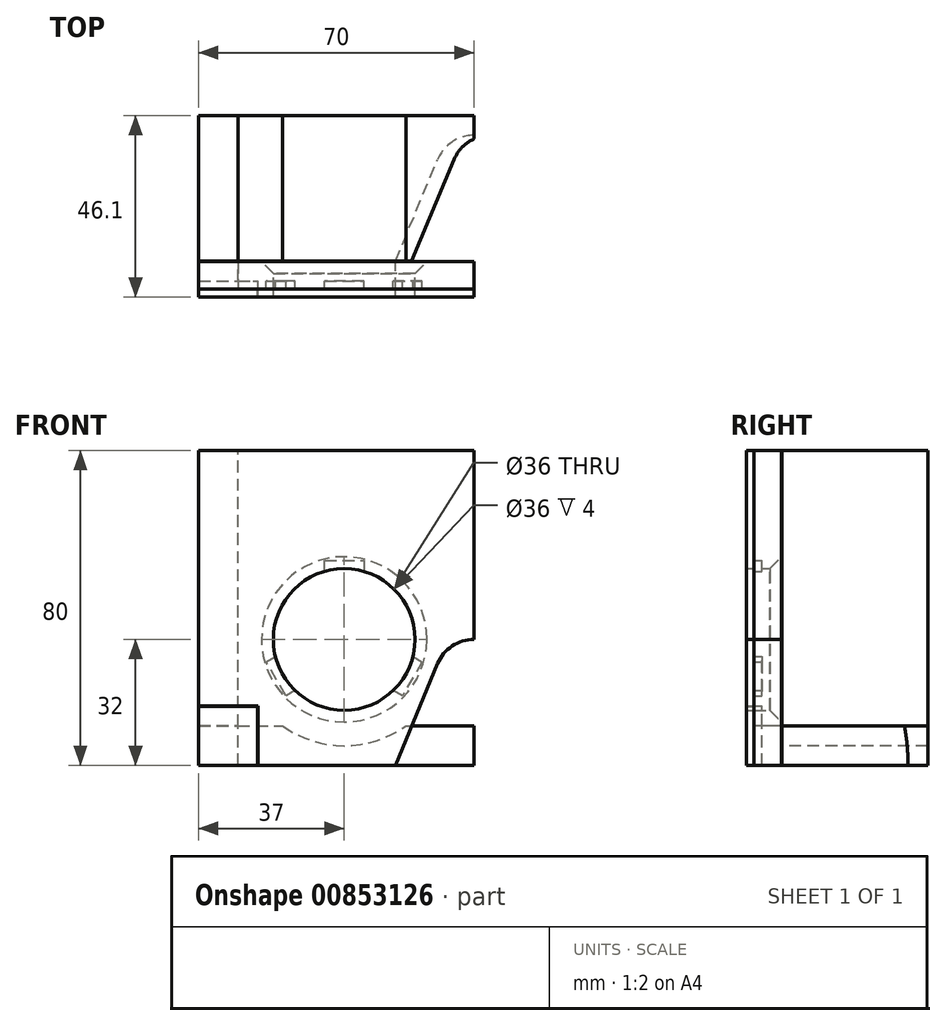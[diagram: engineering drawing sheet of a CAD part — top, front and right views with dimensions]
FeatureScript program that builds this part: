
annotation { "Feature Type Name" : "Feature", "Feature Type Description" : "" }
export const myFeature = defineFeature(function(context is Context, id is Id, definition is map)
    precondition{}
    {
        {
            assignVariable(context, id + "F0", {"name" : "tollerance", "anyValue" : 0.1});
        }
        {
            var Q0;
            Q0=qCreatedBy(makeId("Front.planeOp"),FACE);
            var sketch = newSketch(context, id + "F1", { "sketchPlane" : qUnion([Q0])});
            skCircle(sketch, "E0", {"center": v(-33, 0) * mm, "radius": 18 * mm});
            skCircle(sketch, "E1", {"center": v(33, 0) * mm, "radius": 18 * mm});
            skLineSegment(sketch, "E2", {"start": v(-33, 0) * mm, "end": v(0, 0) * mm, "construction": true});
            skLineSegment(sketch, "E3", {"start": v(0, 0) * mm, "end": v(33, 0) * mm, "construction": true});
            skSolve(sketch);
        }
        {
            var Q0;
            Q0=qCreatedBy(makeId("Front.planeOp"),FACE);
            var sketch = newSketch(context, id + "F2", { "sketchPlane" : qUnion([Q0])});
            skCircle(sketch, "E4", {"center": v(-33, 0) * mm, "radius": 18 * mm});
            skLineSegment(sketch, "E5", {"start": v(-38, 17.3) * mm, "end": v(-38, 20) * mm});
            skLineSegment(sketch, "E6", {"start": v(-38, 20) * mm, "end": v(-33, 20) * mm});
            skLineSegment(sketch, "E7", {"start": v(-33, 20) * mm, "end": v(-28, 20) * mm});
            skLineSegment(sketch, "E8", {"start": v(-28, 20) * mm, "end": v(-28, 17.3) * mm});
            skLineSegment(sketch, "E9.1.0", {"start": v(-45.47, -12.98) * mm, "end": v(-47.82, -14.33) * mm});
            skLineSegment(sketch, "E9.1.1", {"start": v(-47.82, -14.33) * mm, "end": v(-50.32, -10) * mm});
            skLineSegment(sketch, "E9.1.2", {"start": v(-50.32, -10) * mm, "end": v(-52.82, -5.67) * mm});
            skLineSegment(sketch, "E9.1.3", {"start": v(-52.82, -5.67) * mm, "end": v(-50.47, -4.32) * mm});
            skLineSegment(sketch, "E9.2.0", {"start": v(-15.53, -4.32) * mm, "end": v(-13.18, -5.67) * mm});
            skLineSegment(sketch, "E9.2.1", {"start": v(-13.18, -5.67) * mm, "end": v(-15.68, -10) * mm});
            skLineSegment(sketch, "E9.2.2", {"start": v(-15.68, -10) * mm, "end": v(-18.18, -14.33) * mm});
            skLineSegment(sketch, "E9.2.3", {"start": v(-18.18, -14.33) * mm, "end": v(-20.53, -12.98) * mm});
            skLineSegment(sketch, "E10", {"start": v(0, 48) * mm, "end": v(-70, 48) * mm});
            skLineSegment(sketch, "E11", {"start": v(-70, 48) * mm, "end": v(-70, -32) * mm});
            skLineSegment(sketch, "E12", {"start": v(-70, -32) * mm, "end": v(-26.67, -32) * mm});
            skArc(sketch, "E13", {"start": v(-26.67, -32) * mm, "mid": v(-21.12, -30.32) * mm, "end": v(-17.44, -25.85) * mm, "construction": true});
            skLineSegment(sketch, "E14", {"start": v(-17.44, -25.85) * mm, "end": v(-9.23, -6.15) * mm});
            skArc(sketch, "E15", {"start": v(0, 0) * mm, "mid": v(-5.55, -1.68) * mm, "end": v(-9.23, -6.15) * mm});
            skLineSegment(sketch, "E16", {"start": v(-17.44, -25.85) * mm, "end": v(-20, -32) * mm});
            skLineSegment(sketch, "E17.bottom", {"start": v(-70, -32) * mm, "end": v(-60, -32) * mm});
            skLineSegment(sketch, "E17.top", {"start": v(-70, -22) * mm, "end": v(-60, -22) * mm});
            skLineSegment(sketch, "E17.left", {"start": v(-70, -32) * mm, "end": v(-70, -22) * mm});
            skLineSegment(sketch, "E17.right", {"start": v(-60, -32) * mm, "end": v(-60, -22) * mm});
            skLineSegment(sketch, "E18", {"start": v(0, 0) * mm, "end": v(0, 48) * mm});
            skLineSegment(sketch, "E19.bottom", {"start": v(-70, -32) * mm, "end": v(-59.9, -32) * mm});
            skLineSegment(sketch, "E19.top", {"start": v(-70, -21.9) * mm, "end": v(-59.9, -21.9) * mm});
            skLineSegment(sketch, "E19.left", {"start": v(-70, -32) * mm, "end": v(-70, -21.9) * mm});
            skLineSegment(sketch, "E19.right", {"start": v(-59.9, -32) * mm, "end": v(-59.9, -21.9) * mm});
            skLineSegment(sketch, "E20", {"start": v(-26.67, -32) * mm, "end": v(-20, -32) * mm});
            skSolve(sketch);
        }
        {
            var Q0;
            {var subQ6=sQuery(id+"F2.wireOp",EDGE,"E5");Q0=makeQuery(id+"F2.imprint","IMPRINT",FACE,{"disambiguationData":[TD([[makeQuery(id+"F2.imprint","IMPRINT",EDGE,{"derivedFrom":subQ6}),1.0]])]});}
            extrude(context, id + "F3", {"entities" : qUnion([Q0]), "depth" : 2 * mm, "offsetDistance" : 25 * mm});
        }
        {
            var Q0;
            {var subQ6=sQuery(id+"F2.wireOp",EDGE,"E5");Q0=makeQuery(id+"F2.imprint","IMPRINT",FACE,{"disambiguationData":[TD([[makeQuery(id+"F2.imprint","IMPRINT",EDGE,{"derivedFrom":subQ6}),1.0]])]});}
            var Q1;
            {var subQ0=sQuery(id+"F2.wireOp",EDGE,"E9.1.0");Q1=makeQuery(id+"F2.imprint","IMPRINT",FACE,{"disambiguationData":[TD([[makeQuery(id+"F2.imprint","IMPRINT",EDGE,{"derivedFrom":subQ0}),-1.0]])]});}
            var Q2;
            {var subQ0=sQuery(id+"F2.wireOp",EDGE,"E9.2.0");Q2=makeQuery(id+"F2.imprint","IMPRINT",FACE,{"disambiguationData":[TD([[makeQuery(id+"F2.imprint","IMPRINT",EDGE,{"derivedFrom":subQ0}),-1.0]])]});}
            var Q3;
            {var subQ0=sQuery(id+"F2.wireOp",EDGE,"E5");Q3=makeQuery(id+"F2.imprint","IMPRINT",FACE,{"disambiguationData":[TD([[makeQuery(id+"F2.imprint","IMPRINT",EDGE,{"derivedFrom":subQ0}),-1.0]])]});}
            extrude(context, id + "F4", {"entities" : qUnion([Q0, Q1, Q2, Q3]), "operationType" : NewBodyOperationType.ADD, "oppositeDirection" : true, "depth" : 5 * mm, "offsetDistance" : 25 * mm});
        }
        {
            var Q0;
            {var subQ6=sQuery(id+"F2.wireOp",EDGE,"E5");Q0=makeQuery(id+"F2.imprint","IMPRINT",FACE,{"disambiguationData":[TD([[makeQuery(id+"F2.imprint","IMPRINT",EDGE,{"derivedFrom":subQ6}),1.0]])]});}
            var Q1;
            {var subQ0=sQuery(id+"F2.wireOp",EDGE,"E9.1.0");Q1=makeQuery(id+"F2.imprint","IMPRINT",FACE,{"disambiguationData":[TD([[makeQuery(id+"F2.imprint","IMPRINT",EDGE,{"derivedFrom":subQ0}),-1.0]])]});}
            var Q2;
            {var subQ0=sQuery(id+"F2.wireOp",EDGE,"E9.2.0");Q2=makeQuery(id+"F2.imprint","IMPRINT",FACE,{"disambiguationData":[TD([[makeQuery(id+"F2.imprint","IMPRINT",EDGE,{"derivedFrom":subQ0}),-1.0]])]});}
            var Q3;
            {var subQ0=sQuery(id+"F2.wireOp",EDGE,"E5");Q3=makeQuery(id+"F2.imprint","IMPRINT",FACE,{"disambiguationData":[TD([[makeQuery(id+"F2.imprint","IMPRINT",EDGE,{"derivedFrom":subQ0}),-1.0]])]});}
            extrude(context, id + "F5", {"entities" : qUnion([Q0, Q1, Q2, Q3]), "depth" : 4 * mm, "offsetDistance" : 25 * mm, "hasSecondDirection" : true, "secondDirectionOppositeDirection" : false, "secondDirectionDepth" : 2 * mm});
        }
        {
            var Q0;
            Q0=makeQuery(id+"FISosbWUcZb33Zc_2.opPattern","COPY",EDGE,{"derivedFrom":makeQuery(id+"F4.opExtrude","CAP_EDGE",EDGE,{"disambiguationData":[OSD([sQuery(id+"F2.wireOp",EDGE,"E4")])],"isStart":false}),"instanceName":"1"});
            var Q1;
            Q1=makeQuery(id+"F4.opExtrude","CAP_EDGE",EDGE,{"disambiguationData":[OSD([sQuery(id+"F2.wireOp",EDGE,"E4")])],"isStart":false});
            chamfer(context, id + "F6", {"entities" : qUnion([Q0, Q1]), "width" : 3 * mm, "tangentPropagation" : true});
        }
        {
            var Q0;
            Q0=qCreatedBy(makeId("Front.planeOp"),FACE);
            var sketch = newSketch(context, id + "F7", { "sketchPlane" : qUnion([Q0])});
            skLineSegment(sketch, "E21.bottom", {"start": v(-70, -32) * mm, "end": v(-55, -32) * mm});
            skLineSegment(sketch, "E21.top", {"start": v(-70, -17) * mm, "end": v(-55, -17) * mm});
            skLineSegment(sketch, "E21.left", {"start": v(-70, -32) * mm, "end": v(-70, -17) * mm});
            skLineSegment(sketch, "E21.right", {"start": v(-55, -32) * mm, "end": v(-55, -17) * mm});
            skLineSegment(sketch, "E22.bottom", {"start": v(-70, -32) * mm, "end": v(-54.9, -32) * mm});
            skLineSegment(sketch, "E22.top", {"start": v(-70, -16.9) * mm, "end": v(-54.9, -16.9) * mm});
            skLineSegment(sketch, "E22.left", {"start": v(-70, -32) * mm, "end": v(-70, -16.9) * mm});
            skLineSegment(sketch, "E22.right", {"start": v(-54.9, -32) * mm, "end": v(-54.9, -16.9) * mm});
            skSolve(sketch);
        }
        {
            var Q0;
            Q0=makeQuery(id+"F7.imprint","IMPRINT",FACE,{"disambiguationData":[TD([[makeQuery(id+"F7.imprint","IMPRINT",EDGE,{"derivedFrom":sQuery(id+"F7.wireOp",EDGE,"E21.bottom")}),1.0]])]});
            var Q1;
            Q1=makeQuery(id+"F7.imprint","IMPRINT",FACE,{"disambiguationData":[TD([[makeQuery(id+"F7.imprint","IMPRINT",EDGE,{"derivedFrom":sQuery(id+"F7.wireOp",EDGE,"E21.top")}),1.0]])]});
            extrude(context, id + "F8", {"entities" : qUnion([Q0, Q1]), "operationType" : NewBodyOperationType.REMOVE, "depth" : 4 * mm, "offsetDistance" : 25 * mm});
        }
        {
            var Q0;
            Q0=makeQuery(id+"F7.imprint","IMPRINT",FACE,{"disambiguationData":[TD([[makeQuery(id+"F7.imprint","IMPRINT",EDGE,{"derivedFrom":sQuery(id+"F7.wireOp",EDGE,"E21.bottom")}),1.0]])]});
            extrude(context, id + "F9", {"entities" : qUnion([Q0]), "depth" : 4 * mm, "offsetDistance" : 25 * mm, "hasSecondDirection" : true, "secondDirectionOppositeDirection" : false, "secondDirectionDepth" : 2 * mm});
        }
        {
            var Q0;
            {var subQ0=sQuery(id+"F2.wireOp",EDGE,"E17.top");Q0=makeQuery(id+"F2.imprint","IMPRINT",FACE,{"disambiguationData":[TD([[makeQuery(id+"F2.imprint","IMPRINT",EDGE,{"derivedFrom":subQ0}),-1.0]])]});}
            extrude(context, id + "F10", {"entities" : qUnion([Q0]), "operationType" : NewBodyOperationType.ADD, "oppositeDirection" : true, "depth" : (5 + getVariable(context, 'tollerance')) * mm, "offsetDistance" : 25 * mm, "hasSecondDirection" : true, "secondDirectionOppositeDirection" : false, "secondDirectionDepth" : 2 * mm});
        }
        {
            var Q0;
            Q0=makeQuery(id+"F10.opExtrude","CAP_FACE",FACE,{"disambiguationData":[OSD([sQuery(id+"F2.wireOp",EDGE,"E17.top"),sQuery(id+"F2.wireOp",EDGE,"E17.right"),sQuery(id+"F2.wireOp",EDGE,"E19.bottom"),sQuery(id+"F2.wireOp",EDGE,"E19.left")])],"isStart":false});
            var sketch = newSketch(context, id + "F11", { "sketchPlane" : qUnion([Q0])});
            skLineSegment(sketch, "E23.bottom", {"start": v(70, -32) * mm, "end": v(60, -32) * mm});
            skLineSegment(sketch, "E23.top", {"start": v(70, 48) * mm, "end": v(60, 48) * mm});
            skLineSegment(sketch, "E23.left", {"start": v(70, -32) * mm, "end": v(70, 48) * mm});
            skLineSegment(sketch, "E23.right", {"start": v(60, -32) * mm, "end": v(60, 48) * mm});
            skLineSegment(sketch, "E24.bottom", {"start": v(60, -32) * mm, "end": v(0, -32) * mm});
            skLineSegment(sketch, "E24.top", {"start": v(60, -22) * mm, "end": v(0, -22) * mm});
            skLineSegment(sketch, "E24.left", {"start": v(60, -32) * mm, "end": v(60, -22) * mm});
            skLineSegment(sketch, "E24.right", {"start": v(0, -32) * mm, "end": v(0, -22) * mm});
            skCircle(sketch, "E25", {"center": v(33, 0) * mm, "radius": 27 * mm});
            skSolve(sketch);
        }
        {
            var Q0;
            Q0=makeQuery(id+"F11.imprint","IMPRINT",FACE,{"disambiguationData":[TD([[makeQuery(id+"F11.imprint","IMPRINT",EDGE,{"derivedFrom":sQuery(id+"F11.wireOp",EDGE,"E24.bottom")}),-1.0]])]});
            var Q1;
            {var subQ1=sQuery(id+"F11.wireOp",EDGE,"E23.top");Q1=makeQuery(id+"F11.imprint","IMPRINT",FACE,{"disambiguationData":[TD([[makeQuery(id+"F11.imprint","IMPRINT",EDGE,{"derivedFrom":subQ1}),1.0]])]});}
            var Q2;
            {var subQ0=sQuery(id+"F11.wireOp",EDGE,"E23.bottom");Q2=makeQuery(id+"F11.imprint","IMPRINT",FACE,{"disambiguationData":[TD([[makeQuery(id+"F11.imprint","IMPRINT",EDGE,{"derivedFrom":subQ0}),-1.0]])]});}
            extrude(context, id + "F12", {"entities" : qUnion([Q0, Q1, Q2]), "operationType" : NewBodyOperationType.ADD, "depth" : 37 * mm, "offsetDistance" : 25 * mm});
        }
        {
            var Q0;
            Q0=makeQuery(id+"F12.boolean.opBoolean","MERGE",FACE,{"derivedFrom":[makeQuery(id+"F10.boolean.opBoolean","MERGE",FACE,{"derivedFrom":[makeQuery(id+"F9.opExtrude","SWEPT_FACE",FACE,{"disambiguationData":[OSD([sQuery(id+"F7.wireOp",EDGE,"E21.bottom")])]}),makeQuery(id+"F10.opExtrude","SWEPT_FACE",FACE,{"disambiguationData":[OSD([sQuery(id+"F2.wireOp",EDGE,"E19.bottom")])]})]}),makeQuery(id+"F12.opExtrude","SWEPT_FACE",FACE,{"disambiguationData":[OSD([sQuery(id+"F11.wireOp",EDGE,"E23.bottom"),sQuery(id+"F11.wireOp",EDGE,"E24.bottom")])]})]});
            var sketch = newSketch(context, id + "F13", { "sketchPlane" : qUnion([Q0])});
            skLineSegment(sketch, "E26", {"start": v(-20, -5.1) * mm, "end": v(-9.23, -30.95) * mm});
            skArc(sketch, "E27", {"start": v(-9.23, -30.95) * mm, "mid": v(-5.55, -35.42) * mm, "end": v(0, -37.1) * mm});
            skLineSegment(sketch, "E28", {"start": v(-20, -5.1) * mm, "end": v(0, -5.1) * mm});
            skLineSegment(sketch, "E29", {"start": v(0, -5.1) * mm, "end": v(0, -37.1) * mm});
            skSolve(sketch);
        }
        {
            var Q0;
            Q0=makeQuery(id+"F13.imprint","IMPRINT",FACE,{"disambiguationData":[TD([[makeQuery(id+"F13.imprint","IMPRINT",EDGE,{"derivedFrom":sQuery(id+"F13.wireOp",EDGE,"E26")}),1.0]])]});
            var Q1;
            Q1=makeQuery(id+"F4.opExtrude","CAP_EDGE",EDGE,{"disambiguationData":[OSD([sQuery(id+"F2.wireOp",EDGE,"E14"),sQuery(id+"F2.wireOp",EDGE,"E16")])],"isStart":false});
            sweep(context, id + "F14", {"operationType" : NewBodyOperationType.REMOVE, "profiles" : qUnion([Q0]), "path" : qUnion([Q1])});
        }
    });
